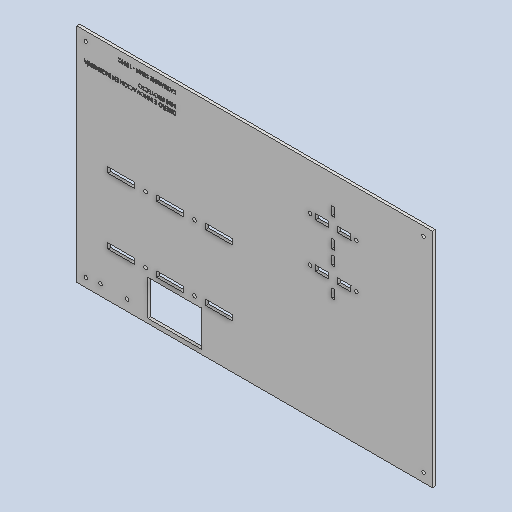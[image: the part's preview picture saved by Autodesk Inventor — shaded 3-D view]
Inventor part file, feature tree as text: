
AUTODESK INVENTOR PART (.ipt)
format: ipt  version: 2022 (Build 260153000, 153)  size: 1,060,864 bytes
history: native  units: mm
features: reference x75, other x8, sketch x4, extrude x3, emboss x1
ambient origin geometry x8: Origin, YZ Plane, XZ Plane, XY Plane, X Axis, Y Axis, Z Axis, Center Point
bodies: Solid1 (feature_tree)
feature tree (91):
  extrude  "Extrusion1"  Depth=250.0mm
  extrude  "Extrusion2"  Depth=3.2mm
  emboss  "Emboss1"
  extrude  "Extrusion3"  Depth=10.0mm TaperAngle=0.0deg
  sketch  "Sketch1"  dims[d0=400.0mm d1=250.0mm]
  sketch  "Sketch2"  dims[d2=3.2mm d3=0.0mm d4=4.0mm]
  reference  "Reference1"
  reference  "Reference2"
  reference  "Reference3"
  reference  "Reference4"
  reference  "Reference5"
  reference  "Reference6"
  reference  "Reference7"
  reference  "Reference8"
  reference  "Reference9"
  reference  "Reference10"
  reference  "Reference11"
  reference  "Reference12"
  reference  "Reference13"
  reference  "Reference14"
  reference  "Reference15"
  reference  "Reference16"
  reference  "Reference17"
  reference  "Reference18"
  reference  "Reference19"
  reference  "Reference20"
  reference  "Reference21"
  reference  "Reference22"
  reference  "Reference23"
  reference  "Reference24"
  reference  "Reference25"
  reference  "Reference26"
  reference  "Reference27"
  reference  "Reference28"
  reference  "Reference29"
  reference  "Reference30"
  reference  "Reference31"
  reference  "Reference32"
  reference  "Reference33"
  reference  "Reference34"
  reference  "Reference35"
  reference  "Reference36"
  reference  "Reference37"
  reference  "Reference38"
  reference  "Reference39"
  reference  "Reference40"
  reference  "Reference41"
  reference  "Reference42"
  reference  "Reference43"
  reference  "Reference44"
  reference  "Reference45"
  reference  "Reference46"
  reference  "Reference47"
  reference  "Reference48"
  reference  "Reference49"
  reference  "Reference50"
  reference  "Reference51"
  reference  "Reference52"
  reference  "Reference53"
  reference  "Reference54"
  reference  "Reference55"
  reference  "Reference56"
  reference  "Reference57"
  reference  "Reference58"
  reference  "Reference59"
  reference  "Reference60"
  reference  "Reference61"
  reference  "Reference62"
  reference  "Reference63"
  reference  "Reference64"
  reference  "Reference65"
  reference  "Reference66"
  reference  "Reference67"
  reference  "Reference68"
  reference  "Reference69"
  reference  "Reference70"
  reference  "Reference71"
  reference  "Reference72"
  reference  "Reference73"
  reference  "Reference74"
  sketch  "Sketch3"  dims[d5=4.0mm d6=10.0mm d7=0.0mm]
  sketch  "Sketch4"  dims[d8=0.1mm d9=0.0mm d10=60.0mm d11=40.0mm d12=5.0mm d13=80.0mm d14=15.0mm d15=0.0mm d16=4.0mm d17=15.0mm d18=10.0mm d19=4.0mm d20=10.0mm d21=10.0mm]
  reference  "Reference75"
  other  "Assembly_Final.iam"
  other  "Base:2"
  other  "Base:1"
  other  "Caja_Reductora:1"
  other  "Carcasa_CajaR_Lateral1:1"
  other  "Carcasa_CajaR_Lateral1:2"
  other  "Base_Soporte:2"
  other  "Acople_Motor:1"
